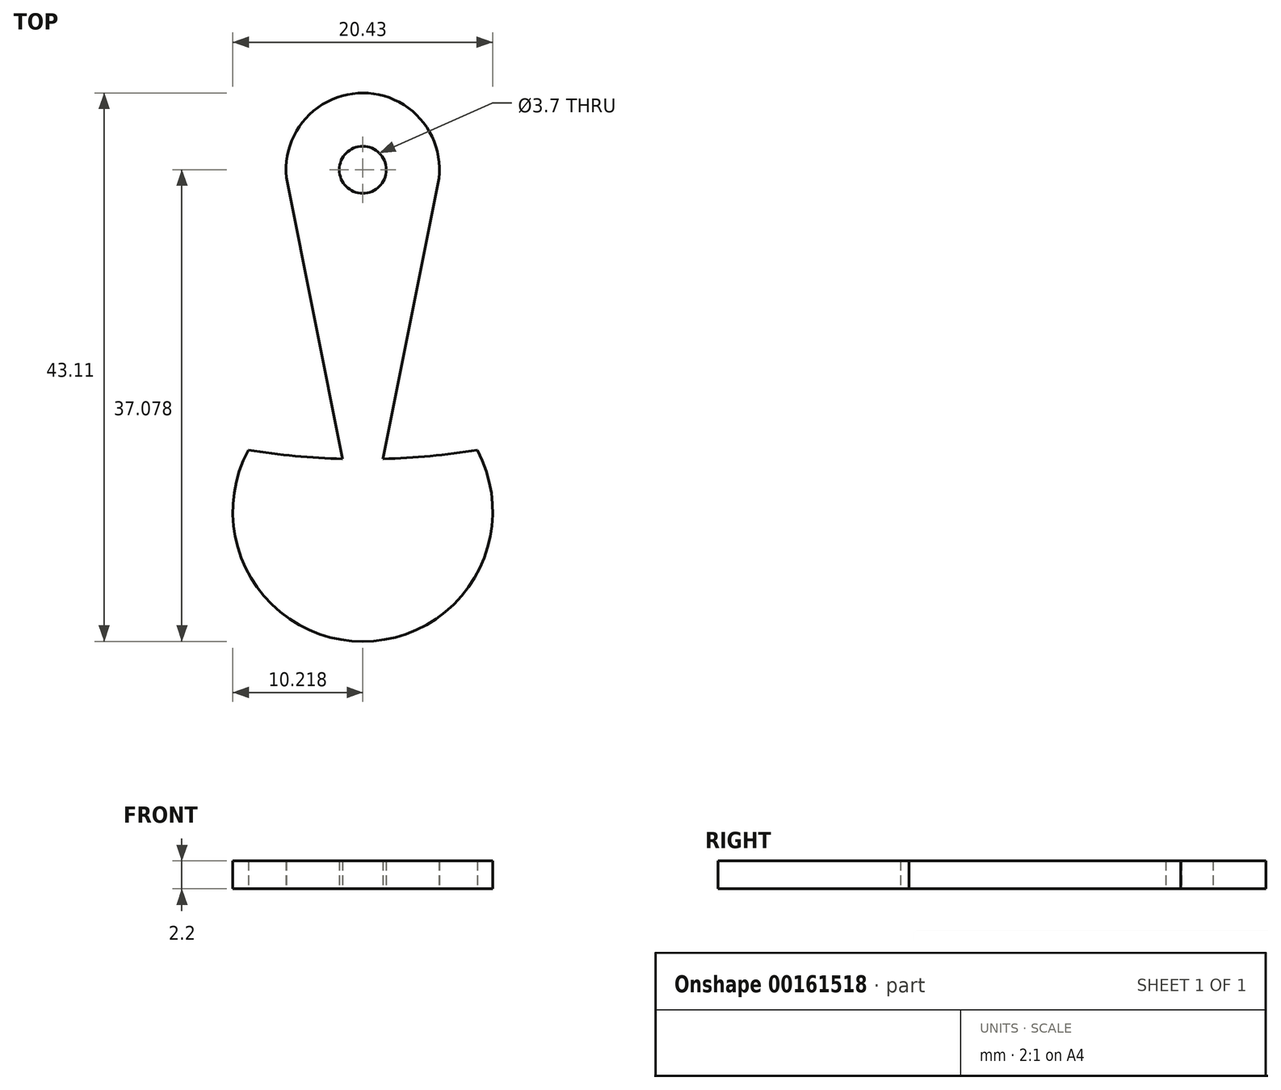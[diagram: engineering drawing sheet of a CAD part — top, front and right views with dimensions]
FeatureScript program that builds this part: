
annotation { "Feature Type Name" : "Feature", "Feature Type Description" : "" }
export const myFeature = defineFeature(function(context is Context, id is Id, definition is map)
    precondition{}
    {
        {
            var Q0;
            Q0=qCreatedBy(makeId("Top.planeOp"),FACE);
            var sketch = newSketch(context, id + "F0", { "sketchPlane" : qUnion([Q0])});
            skLineSegment(sketch, "E0", {"start": v(-55.16, 41.68) * mm, "end": v(-50.65, 19.07) * mm});
            skLineSegment(sketch, "E1", {"start": v(-47.66, 19.07) * mm, "end": v(-43.16, 41.62) * mm});
            skArc(sketch, "E2", {"start": v(-55.16, 41.68) * mm, "mid": v(-49.12, 48.33) * mm, "end": v(-43.16, 41.62) * mm});
            skCircle(sketch, "E3", {"center": v(-49.15, 42.3) * mm, "radius": 1.85 * mm});
            skArc(sketch, "E4", {"start": v(-58.15, 20.27) * mm, "mid": v(-49.15, 5.22) * mm, "end": v(-40.15, 20.27) * mm});
            skArc(sketch, "E5", {"start": v(-58.15, 20.27) * mm, "mid": v(-49.15, 19.55) * mm, "end": v(-40.15, 20.27) * mm});
            skSolve(sketch);
        }
        {
            var Q0;
            Q0=makeQuery(id+"F0.imprint","IMPRINT",FACE,{"disambiguationData":[TD([[makeQuery(id+"F0.imprint","IMPRINT",EDGE,{"derivedFrom":sQuery(id+"F0.wireOp",EDGE,"E0")}),1.0]])]});
            var Q1;
            {var subQ0=sQuery(id+"F0.wireOp",EDGE,"E4");Q1=makeQuery(id+"F0.imprint","IMPRINT",FACE,{"disambiguationData":[TD([[makeQuery(id+"F0.imprint","IMPRINT",EDGE,{"derivedFrom":subQ0}),1.0]])]});}
            extrude(context, id + "F1", {"entities" : qUnion([Q0, Q1]), "depth" : 2.2 * mm});
        }
    });
